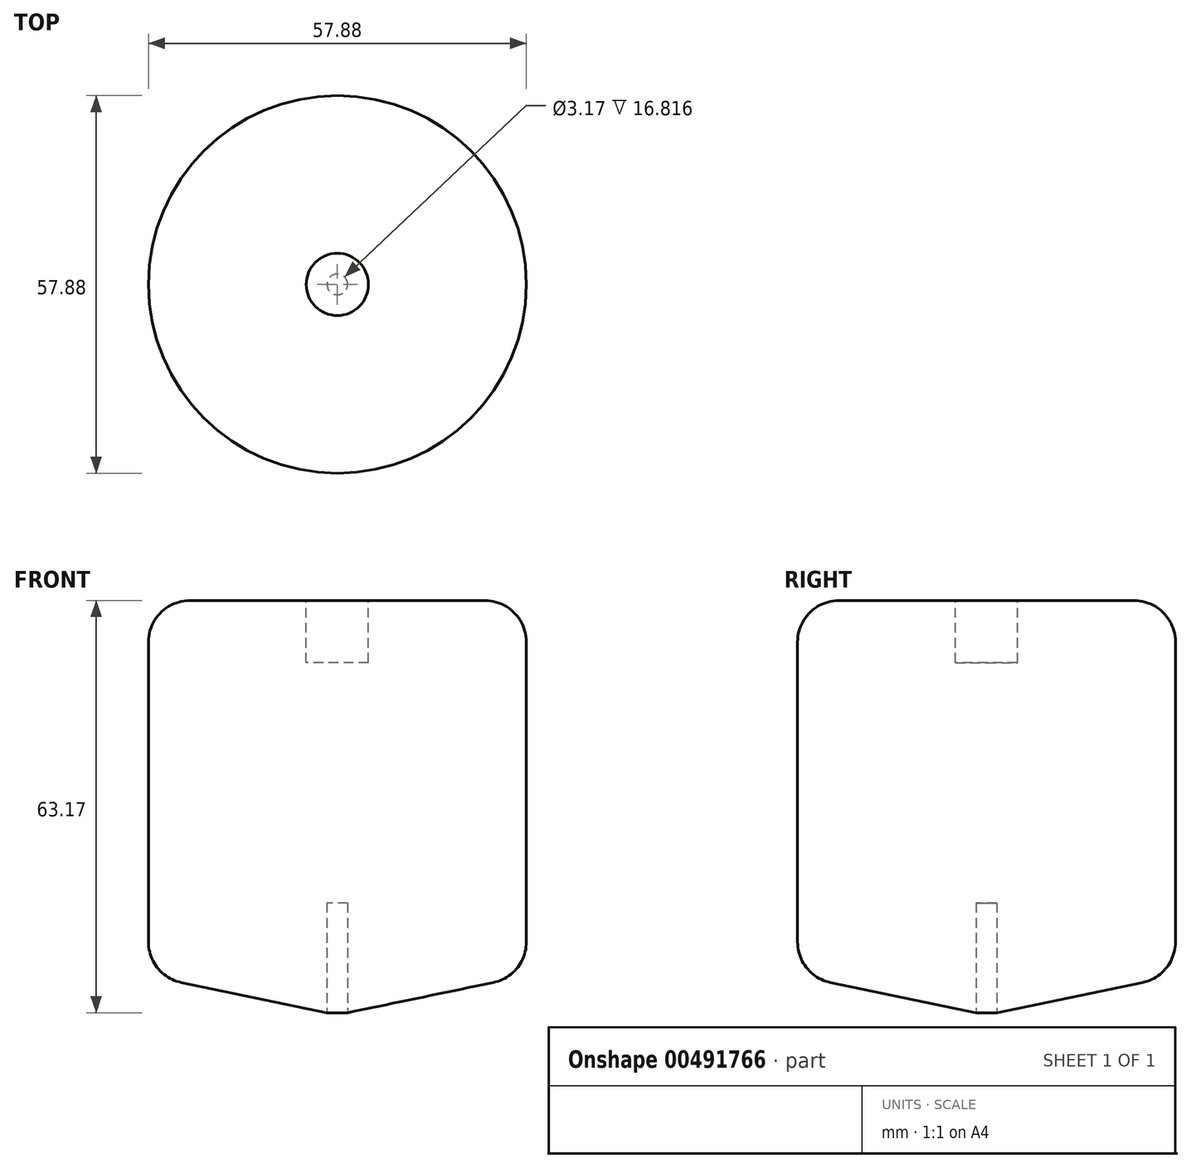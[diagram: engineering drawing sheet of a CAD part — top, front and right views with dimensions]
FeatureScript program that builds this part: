
annotation { "Feature Type Name" : "Feature", "Feature Type Description" : "" }
export const myFeature = defineFeature(function(context is Context, id is Id, definition is map)
    precondition{}
    {
        {
            var Q0;
            Q0=qCreatedBy(makeId("Front.planeOp"),FACE);
            var sketch = newSketch(context, id + "F0", { "sketchPlane" : qUnion([Q0])});
            skLineSegment(sketch, "E0", {"start": v(0, 0) * mm, "end": v(23.88, 4.95) * mm});
            skLineSegment(sketch, "E1", {"start": v(28.94, 11.17) * mm, "end": v(28.94, 57.15) * mm});
            skLineSegment(sketch, "E2", {"start": v(22.59, 63.5) * mm, "end": v(0, 63.5) * mm});
            skLineSegment(sketch, "E3", {"start": v(0, 63.5) * mm, "end": v(0, 0) * mm});
            skPoint(sketch, "E4.visualSharp", {"position": v(28.94, 63.5) * mm});
            skArc(sketch, "E4.filletArc", {"start": v(28.94, 57.15) * mm, "mid": v(27.08, 61.64) * mm, "end": v(22.59, 63.5) * mm});
            skPoint(sketch, "E5.visualSharp", {"position": v(28.94, 6) * mm});
            skArc(sketch, "E5.filletArc", {"start": v(23.88, 4.95) * mm, "mid": v(27.51, 7.16) * mm, "end": v(28.94, 11.17) * mm});
            skSolve(sketch);
        }
        {
            var Q0;
            Q0 = qSketchRegion(id + "F0", true);
            var Q1;
            Q1=sQuery(id+"F0.wireOp",EDGE,"E3");
            revolve(context, id + "F1", {"entities" : qUnion([Q0]), "axis" : qUnion([Q1]), "revolveType" : RevolveType.FULL});
        }
        {
            var Q0;
            Q0=makeQuery(id+"F1.opRevolve","SWEPT_FACE",FACE,{"disambiguationData":[OSD([sQuery(id+"F0.wireOp",EDGE,"E2")])]});
            var sketch = newSketch(context, id + "F2", { "sketchPlane" : qUnion([Q0])});
            skCircle(sketch, "E6", {"center": v(0, 0) * mm, "radius": 4.76 * mm});
            skSolve(sketch);
        }
        {
            var Q0;
            Q0 = qSketchRegion(id + "F2", true);
            extrude(context, id + "F3", {"entities" : qUnion([Q0]), "operationType" : NewBodyOperationType.REMOVE, "oppositeDirection" : true, "depth" : 9.52 * mm});
        }
        {
            var Q0;
            Q0=qCreatedBy(makeId("Top.planeOp"),FACE);
            var sketch = newSketch(context, id + "F4", { "sketchPlane" : qUnion([Q0])});
            skCircle(sketch, "E7", {"center": v(0, 0) * mm, "radius": 1.59 * mm});
            skSolve(sketch);
        }
        {
            var Q0;
            Q0=makeQuery(id+"F4.imprint","IMPRINT",FACE,{"disambiguationData":[TD([[makeQuery(id+"F4.imprint","IMPRINT",EDGE,{"derivedFrom":sQuery(id+"F4.wireOp",EDGE,"E7")}),1.0]])]});
            extrude(context, id + "F5", {"entities" : qUnion([Q0]), "operationType" : NewBodyOperationType.REMOVE, "depth" : 17.14 * mm});
        }
    });
